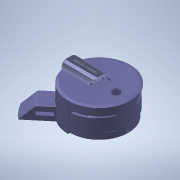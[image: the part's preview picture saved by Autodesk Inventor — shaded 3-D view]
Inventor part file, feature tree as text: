
AUTODESK INVENTOR PART (.ipt)
format: ipt  version: 2020 (Build 240168000, 168)  size: 4,230,656 bytes
history: native  units: mm
features: extrude x60, sketch x25, fillet x22, other x14, plane x11, projected_geometry x8, boolean_combine x7, thread x7, hole x4, revolve x3, shell x3, chamfer x3, move_body x1
ambient origin geometry x8: Origin, YZ Plane, XZ Plane, XY Plane, X Axis, Y Axis, Z Axis, Center Point
bodies: Solid7 (feature_tree), Solid8 (feature_tree), Solid9 (feature_tree), Solid13 (feature_tree)
feature tree (168):
  other  "AroPrincipal"
  extrude  "Extrusion1"  Depth=2.5mm
  sketch  "Sketch3"  dims[d0=90.0mm d1=2.5mm]
  extrude  "Patitas"  Depth=24.43461mm
  revolve  "Revolution1"  [1 undecoded]
  plane  "Work Plane1"
  extrude  "Extrusion3"  Depth=15.0mm
  sketch  "Sketch7"  dims[d7=180.0mm d8=15.0mm]
  revolve  "Revolution2"  [1 undecoded]
  revolve  "Revolution3"  [1 undecoded]
  extrude  "Extrusion4"  Depth=20.0mm
  plane  "Work Plane2"
  extrude  "Extrusion5"  Depth=15.0mm
  extrude  "Extrusion6"  Depth=5.0mm
  plane  "Work Plane3"
  extrude  "Extrusion7"  Depth=7.5mm
  sketch  "Sketch11"  dims[d20=15.0mm d21=15.0mm]
  extrude  "Extrusion10"  TaperAngle=90.0deg  [1 undecoded]
  extrude  "Extrusion11"  Depth=90.0mm
  extrude  "Extrusion17"  Depth=85.0mm
  plane  "Work Plane4"
  move_body  "Move Body2"
  extrude  "Extrusion21"  Depth=16.580628mm
  plane  "Work Plane5"
  extrude  "Extrusion22"  Depth=10.0mm
  plane  "Work Plane6"
  extrude  "Extrusion23"  Depth=20.0mm
  sketch  "Sketch24"  dims[d24=20.0mm d25=7.5mm]
  extrude  "Extrusion24"  Depth=1.0mm
  extrude  "Extrusion25"  Depth=85.0mm
  shell  "Shell1"  Thickness=43.0mm
  shell  "Shell2"  Thickness=96.0mm
  hole  "Hole1"  [1 undecoded]
  hole  "Hole2"  [1 undecoded]
  boolean_combine  "Combine3"
  extrude  "Extrusion26"  Depth=10.0mm TaperAngle=0.0deg
  extrude  "Extrusion27"  Depth=3.0mm
  sketch  "Sketch25"  dims[d26=5.0mm d27=90.0deg]
  extrude  "Extrusion28"  Depth=43.0mm
  plane  "Work Plane7"
  sketch  "Sketch26"  dims[d28=10.0mm d29=90.0mm]
  extrude  "Extrusion30"  Depth=2.5mm TaperAngle=0.0deg
  extrude  "Extrusion31"  Depth=14.2mm
  thread  "Thread2"  [1 undecoded]
  thread  "Thread3"  [1 undecoded]
  thread  "Thread4"  [1 undecoded]
  extrude  "Extrusion32"  Depth=2.0mm
  boolean_combine  "Combine4"
  fillet  "Fillet4"  Radius=4.6mm
  fillet  "Fillet8"  Radius=2.2mm
  fillet  "Fillet9"  Radius=6.0mm
  plane  "Work Plane8"
  sketch  "Sketch30"  dims[d37=20.0mm d38=0.0mm d39=16.580628mm]
  extrude  "Extrusion33"  Depth=6.8mm
  extrude  "Extrusion34"  Depth=20.0mm
  fillet  "fillet hold screw core"  Radius=40.0mm
  extrude  "Extrusion36"  Depth=25.0mm
  fillet  "Fillet11"  Radius=1.1mm
  hole  "Hole3"  [1 undecoded]
  extrude  "Extrusion37"  Depth=8.0mm
  fillet  "Fillet12"  Radius=15.0mm
  plane  "Work Plane9"
  extrude  "Extrusion38"  Depth=5.0mm TaperAngle=0.0deg
  extrude  "Extrusion39"  Depth=31.4mm
  fillet  "Fillet13"  Radius=31.4mm
  fillet  "Fillet14"  Radius=3.5mm
  extrude  "Extrusion40"  Depth=0.5mm
  extrude  "Extrusion41"  Depth=14.2mm
  other  "Battery holder 1"
  extrude  "Battery holder"  Depth=31.4mm
  hole  "Hole4"  [1 undecoded]
  extrude  "Extrusion44"  Depth=6.0mm TaperAngle=0.0deg
  extrude  "Extrusion45"  Depth=96.0mm
  extrude  "Extrusion46"  [1 undecoded]
  extrude  "Extrusion47"  TaperAngle=0.0deg  [1 undecoded]
  extrude  "Extrusion48"  Depth=2.5mm TaperAngle=0.0deg
  extrude  "Extrusion49"  Depth=8.5mm
  extrude  "Extrusion50"  Depth=96.0mm
  extrude  "Extrusion51"  Depth=85.0mm
  extrude  "Extrusion52"  Depth=96.0mm
  fillet  "Fillet15"  Radius=35.0mm
  chamfer  "Chamfer1"  Distance=1.5mm
  sketch  "Sketch36"  dims[d51=10.0mm d52=2.0mm d53=35.0mm d54=4.0mm d55=2.0mm]
  extrude  "Extrusion53"  Depth=2.0mm
  extrude  "Extrusion56"  Depth=2.0mm
  extrude  "Extrusion57"  Depth=3.0mm
  extrude  "Extrusion58"  Depth=30.0mm
  thread  "Thread5"  [1 undecoded]
  thread  "Thread6"  [1 undecoded]
  thread  "Thread7"  [1 undecoded]
  thread  "Thread8"  [1 undecoded]
  chamfer  "Chamfer2"  Distance=35.0mm
  fillet  "Fillet17"  Radius=15.0mm
  other  "tapa PPG"
  other  "tapa up PPG"
  extrude  "Extrusion61"  Depth=30.0mm
  sketch  "Sketch41"  dims[d56=3.0mm d57=96.0mm]
  extrude  "Extrusion66"  Depth=1.5mm
  fillet  "Fillet19"  Radius=14.0mm
  boolean_combine  "Combine5"
  boolean_combine  "Combine6"
  shell  "Shell4"  Thickness=7.0mm
  extrude  "Extrusion67"  Depth=7.0mm
  other  "plano sup sup"
  extrude  "Extrusion68"  Depth=7.0mm
  extrude  "Extrusion69"  Depth=7.0mm
  fillet  "Fillet22"  Radius=12.0mm
  fillet  "Fillet23"  Radius=12.0mm
  fillet  "Fillet24"  Radius=10.0mm
  boolean_combine  "Combine7"
  fillet  "Fillet25"  Radius=12.0mm
  extrude  "Extrusion70"  Depth=2.0mm
  boolean_combine  "Combine8"
  extrude  "Extrusion71"  Depth=1.5mm
  fillet  "Fillet26"  Radius=1.5mm
  fillet  "Fillet28"  Radius=4.0mm
  fillet  "Fillet29"  Radius=2.0mm
  chamfer  "Chamfer3"  Distance=4.0mm
  boolean_combine  "Combine10"
  fillet  "Fillet30"  Radius=2.0mm
  extrude  "Extrusion72"  Depth=14.0mm TaperAngle=0.0deg
  fillet  "Fillet31"  Radius=10.0mm
  fillet  "Fillet32"  Radius=34.0mm
  fillet  "Fillet33"  Radius=10.5mm
  extrude  "Extrusion73"  Depth=0.5mm
  extrude  "Extrusion74"  Depth=10.0mm
  extrude  "Extrusion75"  Depth=2.5mm
  extrude  "Extrusion76"  Depth=36.1mm TaperAngle=0.0deg
  plane  "Work Plane11"
  extrude  "Extrusion77"  [1 undecoded]
  plane  "Work Plane12"
  sketch  "Sketch46"  dims[d66=96.0mm d67=2.5mm d68=0.0mm]
  extrude  "Extrusion78"  Depth=2.5mm
  extrude  "Extrusion79"  Depth=1.5mm
  sketch  "Sketch47"  dims[d78=18.54mm d79=14.2mm d80=15.0mm d81=11.43mm d82=2.0mm d83=2.0mm d84=4.6mm d85=2.2mm d86=6.0mm d87=6.8mm d88=20.0mm d90=40.0mm d91=25.0mm d94=1.1mm d95=12.5mm d96=8.0mm d97=15.0mm d98=0.0mm d110=5.0mm d111=0.0mm d122=31.4mm d123=31.4mm d124=3.5mm d125=0.5mm d126=14.2mm d131=31.4mm d132=16.1mm d139=6.0mm d140=0.0mm d144=96.0mm d145=-48.0mm d152=0.0mm d153=-17.5mm d154=0.0mm d163=2.5mm d164=0.0mm d171=8.5mm d172=96.0mm d173=85.0mm d174=96.0mm d175=35.0mm d176=1.5mm d177=2.0mm d178=2.0mm d179=3.0mm d180=30.0mm d181=2.0mm d182=0.0mm d183=3.0mm d184=85.0mm d185=85.0mm d186=35.0mm d188=15.0mm d189=30.0mm d190=1.5mm d191=14.0mm d192=0.0mm d195=7.0mm d196=7.0mm d197=7.0mm d198=7.0mm d199=12.0mm d200=12.0mm d201=10.0mm d202=0.0mm d203=12.0mm d204=0.0mm d205=2.0mm d206=1.5mm d207=1.5mm d208=7.0mm d209=6.0mm d210=4.0mm d211=2.0mm d212=90.0deg d213=8.0mm d214=20.594885mm d215=7.0mm d216=6.0mm d217=4.0mm d218=2.0mm d219=90.0deg d220=8.0mm d221=20.594885mm d222=4.0mm d223=2.0mm d224=4.0mm d225=2.0mm d226=14.0mm d227=0.0mm d228=10.0mm d229=34.0mm d230=10.5mm d231=0.0mm d232=0.5mm d233=10.0mm d234=2.5mm d235=36.1mm d236=0.0mm d239=-42.5mm d242=2.5mm d243=1.5mm d244=3.0mm d245=2.5mm d246=1.5mm d247=3.0mm d249=0.15mm d251=54.0mm d252=0.0mm d254=10.0mm d255=34.0mm d256=3.0mm d257=3.0mm d258=3.0mm d259=5.0mm d260=5.0mm d261=5.0mm d262=5.0mm d263=5.0mm d264=3.5mm d265=0.0mm d268=3.5mm d269=0.0mm d270=3.5mm d271=0.0mm d272=3.5mm d273=0.0mm d274=3.5mm d275=0.0mm d276=10.0mm d280=5.0mm d282=10.5mm d283=1.0mm d284=0.5mm d285=1.0mm d286=0.75mm d287=6.5mm d288=96.0mm d289=85.0mm d290=96.0mm d291=35.0mm d292=1.5mm d293=2.0mm d294=2.0mm d295=3.0mm d296=30.0mm d297=2.0mm d298=0.0mm d299=25.0mm d300=3.0mm d301=0.0mm d302=10.0mm d303=2.25mm d304=10.0mm d307=2.0mm d308=0.0mm d309=1.5mm d310=3.0mm d311=4.5mm d312=5.0mm d313=3.0mm d314=2.5mm d315=3.0mm d316=5.98424mm d317=3.023mm d318=2.0mm d319=14.3117mm d320=2.0mm d321=0.0mm d322=1.5mm d323=1.5mm d324=58.5mm d325=0.0mm d326=1.0mm d327=0.25mm d328=23.9mm d329=85.0mm d332=1.3mm d333=0.0mm d334=10.0mm d335=5.0mm d336=45.0deg d337=0.4mm d338=0.0mm d339=0.25mm d340=0.2mm d346=0.1mm d347=0.1mm d348=0.1mm d349=1.0mm d350=0.75mm d352=0.5mm d353=1.3mm d354=0.0mm d355=0.5mm d356=0.0mm d357=0.5mm d358=85.0mm d359=90.0deg d360=25.0mm d361=96.0mm d362=38.0mm d367=20.0mm d368=0.0mm d369=1.5mm d370=14.67mm d371=0.0mm d372=20.0mm d373=6.0mm d374=4.0mm d375=2.0mm d376=90.0deg d377=12.67mm d378=0.0mm d381=6.17mm d382=0.0mm d383=4.67mm d384=0.0mm d385=4.67mm d386=0.0mm d387=6.5mm d388=13.438mm d389=3.2mm d390=0.5mm d391=0.7mm d392=13.17mm d393=0.0mm d394=13.17mm d395=0.0mm d396=0.5mm d397=3.25mm d406=0.0mm d409=13.0mm d411=10.0mm d412=0.0mm d413=6.5mm d414=1.5mm d415=1.5mm d416=3.5mm d417=6.5mm d418=1.5mm d419=0.5mm d420=0.7mm d421=2.5mm d422=0.0mm d423=2.5mm d424=0.0mm d425=2.5mm d426=0.0mm d427=2.0mm d428=0.5mm d429=5.0mm d430=7.25mm d431=45.0deg d432=8.0mm d433=20.0mm d434=1.25mm d435=85.0mm d436=20.0mm d437=1.25mm d438=2.0mm d439=0.0mm d440=90.0mm d441=180.0mm d442=85.0mm d443=73.0mm d452=6.0mm d458=2.0mm d459=2.0mm d460=96.0mm d461=2.0mm d462=2.0mm d463=4.0mm d464=8.0mm d465=8.0mm d466=4.0mm d467=4.0mm d468=4.0mm d469=4.0mm d470=6.0mm d471=6.0mm d472=3.0mm d473=3.0mm d474=3.0mm d475=3.0mm d476=5.0mm d477=0.0mm d478=2.0mm d479=0.0mm d480=5.0mm d481=0.0mm d482=3.5mm d483=0.0mm d484=3.5mm d485=0.0mm d486=3.5mm d487=0.0mm d488=3.5mm d489=0.0mm d490=5.0mm d491=2.0mm d492=45.0deg d493=5.0mm d504=15.0mm d512=60.0deg d534=4.0mm d535=2.0mm d536=10.0mm d545=10.0mm d548=15.0mm d549=4.363323mm d550=4.0mm d551=2.0mm d552=10.0mm d553=10.0mm d554=15.0mm d555=2.5mm d558=25.0mm d559=0.0mm d576=96.0mm d577=70.0mm d578=20.0mm d579=7.0mm d580=10.5mm d581=0.0mm d582=8.5mm d583=2.0mm d584=25.0mm d585=0.0mm d586=55.5mm d587=96.0mm d588=70.0mm d589=25.0mm d590=10.0mm d591=0.0mm d592=2.0mm d593=0.0mm d596=177.0mm d597=17.75mm d598=11.0mm d599=17.75mm d600=11.0mm d601=10.0mm d602=10.0mm d603=6.0mm d604=10.0mm d605=0.0mm d606=40.0mm d607=12.5mm d608=0.0mm d609=0.0mm d610=8.0mm d611=2.0mm d612=10.0mm d616=1.0mm d617=2.0mm d618=5.0mm d619=0.5mm d620=4.0mm d621=1.0mm d622=45.0deg d623=1.0mm d624=9.0mm d625=2.75mm d626=40.0mm d627=1.5mm d628=0.0mm d629=0.5mm d630=27.0mm d631=4.0mm d632=1.0mm d633=2.0mm d634=1.0mm d635=1.0mm d636=20.0mm d637=0.0mm d638=15.0mm d639=0.0mm d640=2.5mm d641=0.0mm d642=2.5mm d643=0.0mm d644=-0.5mm d645=0.5mm d646=0.0mm d647=45.5mm d648=35.011113mm d649=13.22mm d650=17.5mm d651=11.2mm d652=1.12mm d653=0.0mm d654=2.5mm d655=0.0mm d656=10.0mm d657=35.0mm d660=2.0mm d661=8.0mm d662=17.5mm d663=4.75mm d664=1.0mm d665=45.0mm d666=0.0mm d667=44.749mm d668=0.0mm d669=2.54mm d670=2.54mm d671=1.0mm]
  extrude  "Extrusion80"  Depth=3.0mm
  extrude  "Extrusion81"  Depth=2.5mm
  sketch  "Sketch5"  dims[d2=43.0mm d3=0.0mm d4=24.43461mm]
  sketch  "Sketch6"  dims[d5=90.0mm d6=6.981317mm]
  other  "Enganche"
  sketch  "Sketch8"  dims[d9=15.0mm d11=20.0mm d12=0.0mm]
  sketch  "Sketch9"  dims[d15=20.0mm d16=90.0mm]
  projected_geometry  "Projected Loop1"
  sketch  "Sketch10"  dims[d18=180.0deg d19=20.0mm]
  other  "tapa"
  projected_geometry  "Projected Loop2"
  other  "Fingertip"
  sketch  "Sketch20"  dims[d22=25.0mm d23=5.0mm]
  other  "inf RR"
  other  "reflector"
  projected_geometry  "Projected Loop7"
  projected_geometry  "Projected Loop8"
  projected_geometry  "Projected Loop9"
  sketch  "Sketch28"  dims[d30=96.0mm d36=85.0mm]
  sketch  "Sketch31"  dims[d40=16.580628mm d41=10.0mm]
  other  "tapa RR"
  sketch  "Sketch32"  dims[d42=2.5mm d43=20.0mm]
  sketch  "Sketch33"  dims[d44=29.84513mm d45=1.0mm]
  sketch  "Sketch34"  dims[d46=0.174533mm d47=85.0mm d48=43.0mm d49=0.0mm d50=96.0mm]
  other  "forma dedo"
  other  "PPG cover"
  sketch  "Sketch42"  dims[d58=2.0mm d59=10.0mm d60=0.0mm]
  other  "forma dedo sup"
  sketch  "Sketch44"  dims[d61=35.0mm d62=3.0mm]
  sketch  "Sketch45"  dims[d63=30.0mm d64=0.0mm d65=43.0mm]
  projected_geometry  "Project Cut Edges1"
  projected_geometry  "Project Cut Edges2"
  projected_geometry  "Project Cut Edges3"
note: 18 required parameter values undecoded (feature->parameter linkage not recoverable at this tier; creation-order binding heuristic only, values carry confidence <= 0.55)